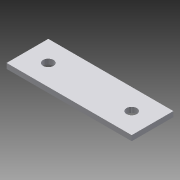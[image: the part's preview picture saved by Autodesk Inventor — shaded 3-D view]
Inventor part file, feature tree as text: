
AUTODESK INVENTOR PART (.ipt)
format: ipt  version: 2015 SP1 (Build 190203100, 203)  size: 99,840 bytes
history: native  units: in
note: dims shown in document units (in); Inventor stores cm internally (conversion verified against a paired STEP export)
features: sketch x2, extrude x1, hole x1
ambient origin geometry x8: Origin, YZ Plane, XZ Plane, XY Plane, X Axis, Y Axis, Z Axis, Center Point
bodies: Solid1 (feature_tree)
feature tree (4):
  extrude  "Extrusion1"  Depth=1.0in
  hole  "Hole1"  [1 undecoded]
  sketch  "Sketch1"  dims[d0=3.0in d1=1.0in]
  sketch  "Sketch2"  dims[d2=0.125in d3=0.0in d4=0.5in d5=0.5in d6=0.5in d7=0.5in d8=0.25in d9=0.75in d10=0.375in d11=0.25in d12=0.5635in d13=1.0in d14=0.8108in]
note: 1 required parameter value undecoded (feature->parameter linkage not recoverable at this tier; creation-order binding heuristic only, values carry confidence <= 0.55)
